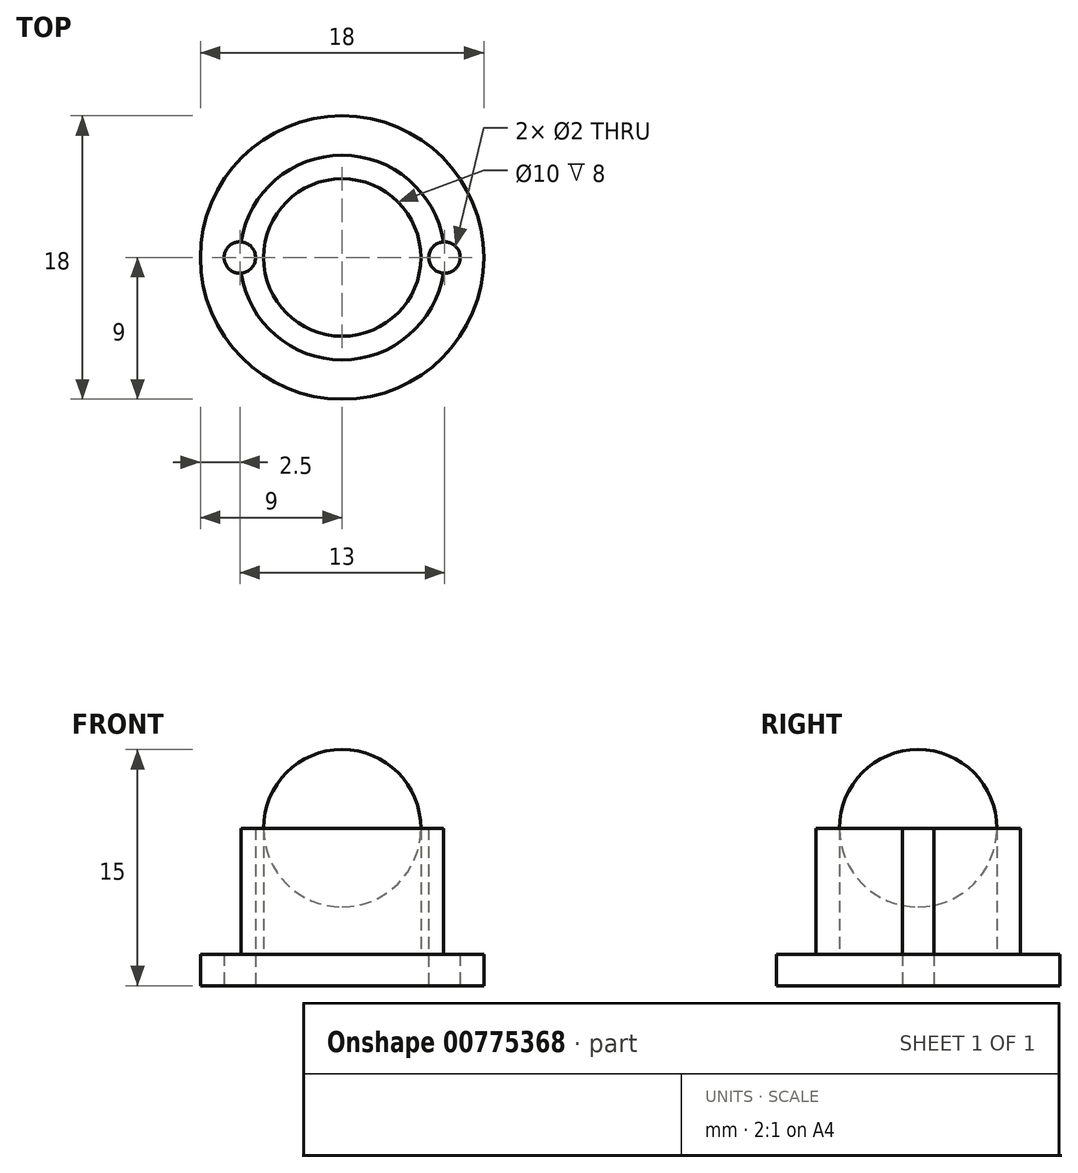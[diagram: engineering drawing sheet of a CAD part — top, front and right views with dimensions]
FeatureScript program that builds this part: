
annotation { "Feature Type Name" : "Feature", "Feature Type Description" : "" }
export const myFeature = defineFeature(function(context is Context, id is Id, definition is map)
    precondition{}
    {
        {
            assignVariable(context, id + "F0", {"name" : "ball_diameter", "anyValue" : 10});
        }
        {
            assignVariable(context, id + "F1", {"name" : "full_height", "anyValue" : 15});
        }
        {
            var Q0;
            Q0=qCreatedBy(makeId("Top.planeOp"),FACE);
            var sketch = newSketch(context, id + "F2", { "sketchPlane" : qUnion([Q0])});
            skCircle(sketch, "E0", {"center": v(6.5, 0) * mm, "radius": 1 * mm});
            skLineSegment(sketch, "E1", {"start": v(0, 0) * mm, "end": v(0, 6.02) * mm, "construction": true});
            skCircle(sketch, "E2.MirrorC", {"center": v(-6.5, 0) * mm, "radius": 1 * mm});
            skCircle(sketch, "E3", {"center": v(0, 0) * mm, "radius": 9 * mm});
            skSolve(sketch);
        }
        {
            var Q0;
            Q0=makeQuery(id+"F2.imprint","IMPRINT",FACE,{"disambiguationData":[TD([[makeQuery(id+"F2.imprint","IMPRINT",EDGE,{"derivedFrom":sQuery(id+"F2.wireOp",EDGE,"E0")}),-1.0]])]});
            extrude(context, id + "F3", {"entities" : qUnion([Q0]), "depth" : 2 * mm, "offsetDistance" : 25 * mm});
        }
        {
            var Q0;
            Q0=qCreatedBy(makeId("Front.planeOp"),FACE);
            var sketch = newSketch(context, id + "F4", { "sketchPlane" : qUnion([Q0])});
            skLineSegment(sketch, "E4", {"start": v(0, 0) * mm, "end": v(0, 16.45) * mm, "construction": true});
            skArc(sketch, "E5", {"start": v(0, 15) * mm, "mid": v(-5, 10) * mm, "end": v(0, 5) * mm});
            skPoint(sketch, "E6", {"position": v(0, 15) * mm});
            skPoint(sketch, "E7", {"position": v(0, 5) * mm});
            skLineSegment(sketch, "E8", {"start": v(0, 15) * mm, "end": v(0, 5) * mm});
            skSolve(sketch);
        }
        {
            var Q0;
            Q0=makeQuery(id+"F4.imprint","IMPRINT",FACE,{"disambiguationData":[TD([[makeQuery(id+"F4.imprint","IMPRINT",EDGE,{"derivedFrom":sQuery(id+"F4.wireOp",EDGE,"E5")}),1.0]])]});
            var Q1;
            Q1=sQuery(id+"F4.wireOp",EDGE,"E4");
            revolve(context, id + "F5", {"surfaceOperationType" : NewSurfaceOperationType.NEW, "entities" : qUnion([Q0]), "axis" : qUnion([Q1]), "revolveType" : RevolveType.FULL});
        }
        {
            var Q0;
            Q0=makeQuery(id+"F3.opExtrude","CAP_FACE",FACE,{"disambiguationData":[OSD([sQuery(id+"F2.wireOp",EDGE,"E0"),sQuery(id+"F2.wireOp",EDGE,"E2.MirrorC"),sQuery(id+"F2.wireOp",EDGE,"E3")])],"isStart":false});
            var sketch = newSketch(context, id + "F6", { "sketchPlane" : qUnion([Q0])});
            skCircle(sketch, "E9", {"center": v(0, 0) * mm, "radius": 6.5 * mm});
            skCircle(sketch, "E10", {"center": v(0, 0) * mm, "radius": 5 * mm});
            skSolve(sketch);
        }
        {
            var Q0;
            Q0=makeQuery(id+"F6.imprint","IMPRINT",FACE,{"disambiguationData":[TD([[makeQuery(id+"F6.imprint","IMPRINT",EDGE,{"derivedFrom":sQuery(id+"F6.wireOp",EDGE,"E10")}),-1.0]])]});
            extrude(context, id + "F7", {"entities" : qUnion([Q0]), "operationType" : NewBodyOperationType.ADD, "depth" : (getVariable(context, 'full_height') - getVariable(context, 'ball_diameter') / 2 - 2) * mm, "offsetDistance" : 25 * mm});
        }
    });
